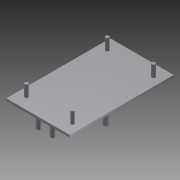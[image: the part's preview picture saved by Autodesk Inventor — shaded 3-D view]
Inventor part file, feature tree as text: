
AUTODESK INVENTOR PART (.ipt)
format: ipt  version: 2012 (Build 160160000, 160)  size: 125,440 bytes
history: native  units: mm
features: extrude x6, sketch x1
ambient origin geometry x8: Origin, YZ Plane, XZ Plane, XY Plane, X Axis, Y Axis, Z Axis, Center Point
bodies: Solid1 (feature_tree)
feature tree (7):
  sketch  "Sketch1"  dims[d0=55.0mm d1=90.0mm d2=4.0mm d3=6.8mm d4=4.0mm d5=4.0mm d6=38.6mm d7=38.6mm d8=4.0mm d9=69.8mm d10=10.0mm d11=80.8mm d12=2.0mm d13=0.0mm d14=15.0mm d15=0.0mm d16=7.0mm d17=0.0mm d18=3.0mm d19=7.5mm d20=10.0mm d21=3.0mm d22=10.0mm d23=7.5mm d24=3.0mm d25=7.5mm d26=10.0mm d27=3.0mm d28=7.5mm d29=10.0mm d30=10.0mm d31=0.0mm d32=10.0mm d33=0.0mm d34=10.0mm d35=0.0mm]
  extrude  "Extrusion1"  Depth=90.0mm
  extrude  "Extrusion2"  Depth=4.0mm
  extrude  "Extrusion3"  Depth=6.8mm
  extrude  "Extrusion4"  Depth=4.0mm
  extrude  "Extrusion5"  Depth=4.0mm
  extrude  "Extrusion6"  Depth=38.6mm
